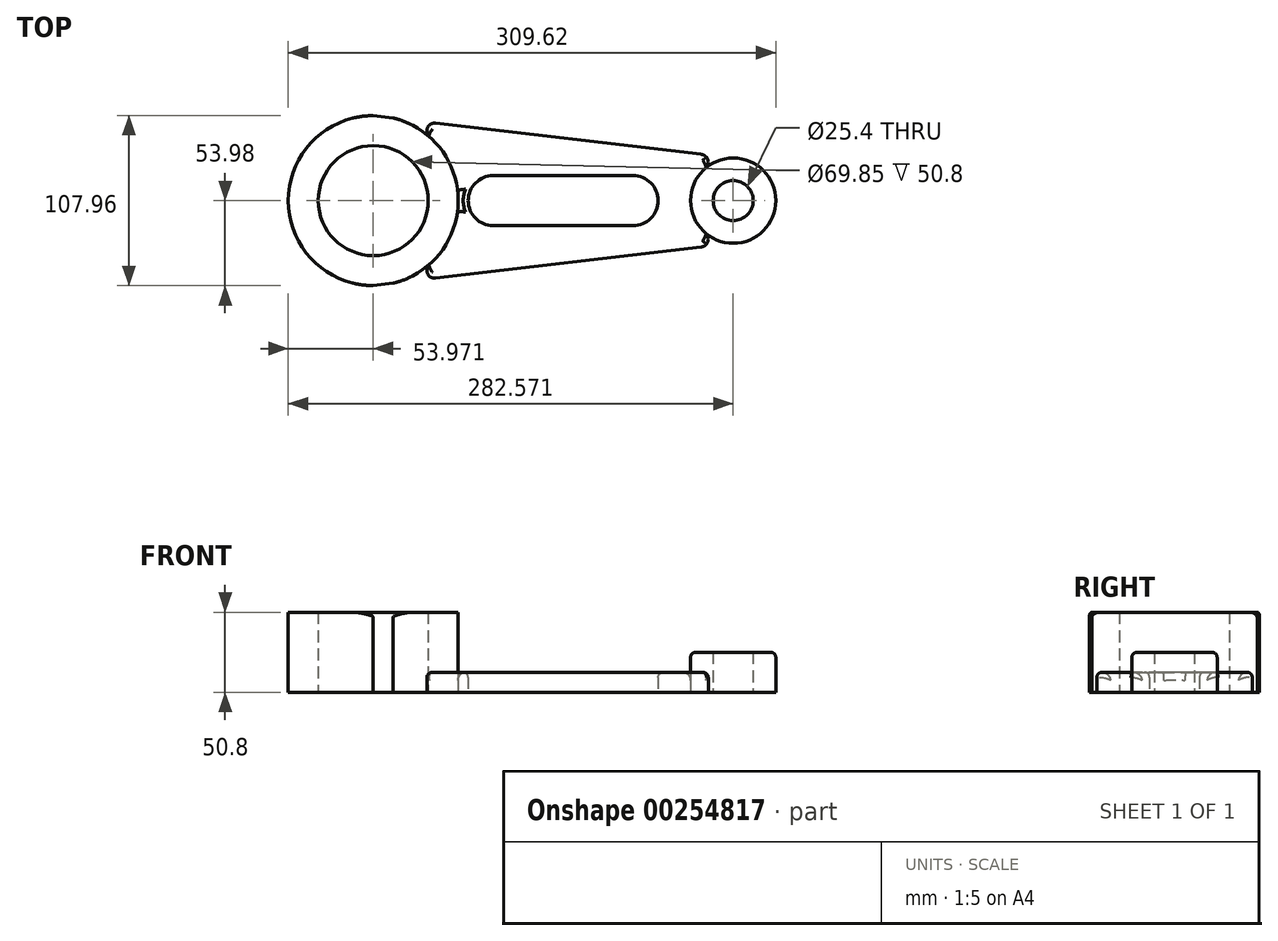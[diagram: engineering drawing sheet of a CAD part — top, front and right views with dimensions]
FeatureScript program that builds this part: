
annotation { "Feature Type Name" : "Feature", "Feature Type Description" : "" }
export const myFeature = defineFeature(function(context is Context, id is Id, definition is map)
    precondition{}
    {
        {
            var Q0;
            Q0=qCreatedBy(makeId("Top.planeOp"),FACE);
            var sketch = newSketch(context, id + "F0", { "sketchPlane" : qUnion([Q0])});
            skCircle(sketch, "E0", {"center": v(-49.03, 0) * mm, "radius": 34.93 * mm});
            skCircle(sketch, "E1", {"center": v(-49.03, 0) * mm, "radius": 53.98 * mm});
            skCircle(sketch, "E2", {"center": v(27.17, 0) * mm, "radius": 15.88 * mm});
            skCircle(sketch, "E3", {"center": v(116.07, 0) * mm, "radius": 15.88 * mm});
            skCircle(sketch, "E4", {"center": v(179.57, 0) * mm, "radius": 12.7 * mm});
            skCircle(sketch, "E5", {"center": v(179.57, 0) * mm, "radius": 27.05 * mm});
            skLineSegment(sketch, "E6", {"start": v(27.17, -15.88) * mm, "end": v(116.07, -15.88) * mm});
            skLineSegment(sketch, "E7", {"start": v(27.17, 15.88) * mm, "end": v(116.07, 15.88) * mm});
            skLineSegment(sketch, "E8", {"start": v(-49.03, 53.97) * mm, "end": v(179.57, 27.05) * mm});
            skLineSegment(sketch, "E9", {"start": v(-49.03, -53.97) * mm, "end": v(179.57, -27.05) * mm});
            skSolve(sketch);
        }
        {
            var Q0;
            Q0=makeQuery(id+"F0.imprint","IMPRINT",FACE,{"disambiguationData":[TD([[makeQuery(id+"F0.imprint","IMPRINT",EDGE,{"derivedFrom":sQuery(id+"F0.wireOp",EDGE,"E0")}),-1.0]])]});
            extrude(context, id + "F1", {"entities" : qUnion([Q0]), "depth" : 50.8 * mm});
        }
        {
            var Q0;
            Q0=makeQuery(id+"F0.imprint","IMPRINT",FACE,{"disambiguationData":[TD([[makeQuery(id+"F0.imprint","IMPRINT",EDGE,{"derivedFrom":sQuery(id+"F0.wireOp",EDGE,"E4")}),-1.0]])]});
            extrude(context, id + "F2", {"entities" : qUnion([Q0]), "depth" : 25.4 * mm});
        }
        {
            var Q0;
            {var subQ5=sQuery(id+"F0.wireOp",EDGE,"E6");Q0=makeQuery(id+"F0.imprint","IMPRINT",FACE,{"disambiguationData":[TD([[makeQuery(id+"F0.imprint","IMPRINT",EDGE,{"derivedFrom":subQ5}),-1.0]])]});}
            extrude(context, id + "F3", {"entities" : qUnion([Q0]), "depth" : 12.7 * mm});
        }
        {
            var Q0;
            Q0=makeQuery(id+"F0.imprint","IMPRINT",FACE,{"disambiguationData":[TD([[makeQuery(id+"F0.imprint","IMPRINT",EDGE,{"derivedFrom":sQuery(id+"F0.wireOp",EDGE,"E0")}),1.0]])]});
            extrude(context, id + "F4", {"entities" : qUnion([Q0]), "operationType" : NewBodyOperationType.REMOVE, "oppositeDirection" : true, "depth" : 25.4 * mm});
        }
        {
            var Q0;
            {var subQ0=sQuery(id+"F0.wireOp",EDGE,"E6");Q0=makeQuery(id+"F0.imprint","IMPRINT",FACE,{"disambiguationData":[TD([[makeQuery(id+"F0.imprint","IMPRINT",EDGE,{"derivedFrom":subQ0}),1.0]])]});}
            var Q1;
            {var subQ0=sQuery(id+"F0.wireOp",EDGE,"E2");var subQ1=makeQuery(id+"F0.imprint","INTERSECT",VERTEX,{"derivedFrom":[subQ0,sQuery(id+"F0.wireOp",EDGE,"E6")]});Q1=makeQuery(id+"F0.imprint","IMPRINT",FACE,{"disambiguationData":[TD([[makeQuery(id+"F0.imprint","IMPRINT",EDGE,{"disambiguationData":[TD([[subQ1,1.0]])],"derivedFrom":subQ0}),1.0]])]});}
            var Q2;
            {var subQ0=sQuery(id+"F0.wireOp",EDGE,"E3");var subQ1=makeQuery(id+"F0.imprint","INTERSECT",VERTEX,{"derivedFrom":[subQ0,sQuery(id+"F0.wireOp",EDGE,"E6")]});Q2=makeQuery(id+"F0.imprint","IMPRINT",FACE,{"disambiguationData":[TD([[makeQuery(id+"F0.imprint","IMPRINT",EDGE,{"disambiguationData":[TD([[subQ1,1.0]])],"derivedFrom":subQ0}),1.0]])]});}
            extrude(context, id + "F5", {"entities" : qUnion([Q0, Q1, Q2]), "operationType" : NewBodyOperationType.REMOVE, "oppositeDirection" : true, "depth" : 25.4 * mm});
        }
        {
            var Q0;
            Q0=makeQuery(id+"F0.imprint","IMPRINT",FACE,{"disambiguationData":[TD([[makeQuery(id+"F0.imprint","IMPRINT",EDGE,{"derivedFrom":sQuery(id+"F0.wireOp",EDGE,"E4")}),1.0]])]});
            extrude(context, id + "F6", {"entities" : qUnion([Q0]), "operationType" : NewBodyOperationType.REMOVE, "oppositeDirection" : true, "depth" : 25.4 * mm});
        }
        {
            var Q0;
            {var subQ0=sQuery(id+"F0.wireOp",EDGE,"E1");Q0=makeQuery(id+"F1.opExtrude","CAP_EDGE",EDGE,{"disambiguationData":[OSD([subQ0]),TDD([makeQuery(id+"F0.imprint","IMPRINT",EDGE,{"disambiguationData":[TD([[makeQuery(id+"F0.imprint","INTERSECT",VERTEX,{"disambiguationData":[OD(0.0)],"derivedFrom":[subQ0,sQuery(id+"F0.wireOp",EDGE,"E8")]}),-1.0]])],"derivedFrom":subQ0})])],"isStart":false});}
            var Q1;
            {var subQ0=sQuery(id+"F0.wireOp",EDGE,"E1");Q1=makeQuery(id+"F1.opExtrude","CAP_EDGE",EDGE,{"disambiguationData":[OSD([subQ0]),TDD([makeQuery(id+"F0.imprint","IMPRINT",EDGE,{"disambiguationData":[TD([[makeQuery(id+"F0.imprint","INTERSECT",VERTEX,{"disambiguationData":[OD(1.0)],"derivedFrom":[subQ0,sQuery(id+"F0.wireOp",EDGE,"E8")]}),1.0]])],"derivedFrom":subQ0})])],"isStart":false});}
            var Q2;
            Q2=makeQuery(id+"F1.opExtrude","CAP_EDGE",EDGE,{"disambiguationData":[OSD([sQuery(id+"F0.wireOp",EDGE,"E9")])],"isStart":false});
            var Q3;
            Q3=makeQuery(id+"F1.opExtrude","CAP_EDGE",EDGE,{"disambiguationData":[OSD([sQuery(id+"F0.wireOp",EDGE,"E8")])],"isStart":false});
            fillet(context, id + "F7", {"entities" : qUnion([Q0, Q1, Q2, Q3]), "radius" : 3.17 * mm, "tangentPropagation" : true, "allowEdgeOverflow" : false});
        }
        {
            var Q0;
            Q0=makeQuery(id+"F2.opExtrude","CAP_EDGE",EDGE,{"disambiguationData":[OSD([sQuery(id+"F0.wireOp",EDGE,"E5")])],"isStart":false});
            fillet(context, id + "F8", {"entities" : qUnion([Q0]), "radius" : 3.17 * mm, "tangentPropagation" : true, "allowEdgeOverflow" : false});
        }
        {
            var Q0;
            Q0=makeQuery(id+"F3.opExtrude","CAP_EDGE",EDGE,{"disambiguationData":[OSD([sQuery(id+"F0.wireOp",EDGE,"E9")])],"isStart":false});
            var Q1;
            Q1=makeQuery(id+"F3.opExtrude","CAP_EDGE",EDGE,{"disambiguationData":[OSD([sQuery(id+"F0.wireOp",EDGE,"E2")])],"isStart":false});
            var Q2;
            Q2=makeQuery(id+"F3.opExtrude","CAP_EDGE",EDGE,{"disambiguationData":[OSD([sQuery(id+"F0.wireOp",EDGE,"E6")])],"isStart":false});
            var Q3;
            Q3=makeQuery(id+"F3.opExtrude","CAP_EDGE",EDGE,{"disambiguationData":[OSD([sQuery(id+"F0.wireOp",EDGE,"E8")])],"isStart":false});
            fillet(context, id + "F9", {"entities" : qUnion([Q0, Q1, Q2, Q3]), "radius" : 3.17 * mm, "tangentPropagation" : true, "allowEdgeOverflow" : false});
        }
        {
            var Q0;
            Q0=makeQuery(id+"F3.opExtrude","CAP_EDGE",EDGE,{"disambiguationData":[OSD([sQuery(id+"F0.wireOp",EDGE,"E1")])],"isStart":false});
            fillet(context, id + "F10", {"entities" : qUnion([Q0]), "radius" : 5.08 * mm, "tangentPropagation" : true, "allowEdgeOverflow" : false});
        }
        {
            var Q0;
            Q0=makeQuery(id+"F3.opExtrude","CAP_EDGE",EDGE,{"disambiguationData":[OSD([sQuery(id+"F0.wireOp",EDGE,"E5")])],"isStart":false});
            fillet(context, id + "F11", {"entities" : qUnion([Q0]), "radius" : 5.08 * mm, "tangentPropagation" : true, "allowEdgeOverflow" : false});
        }
    });
